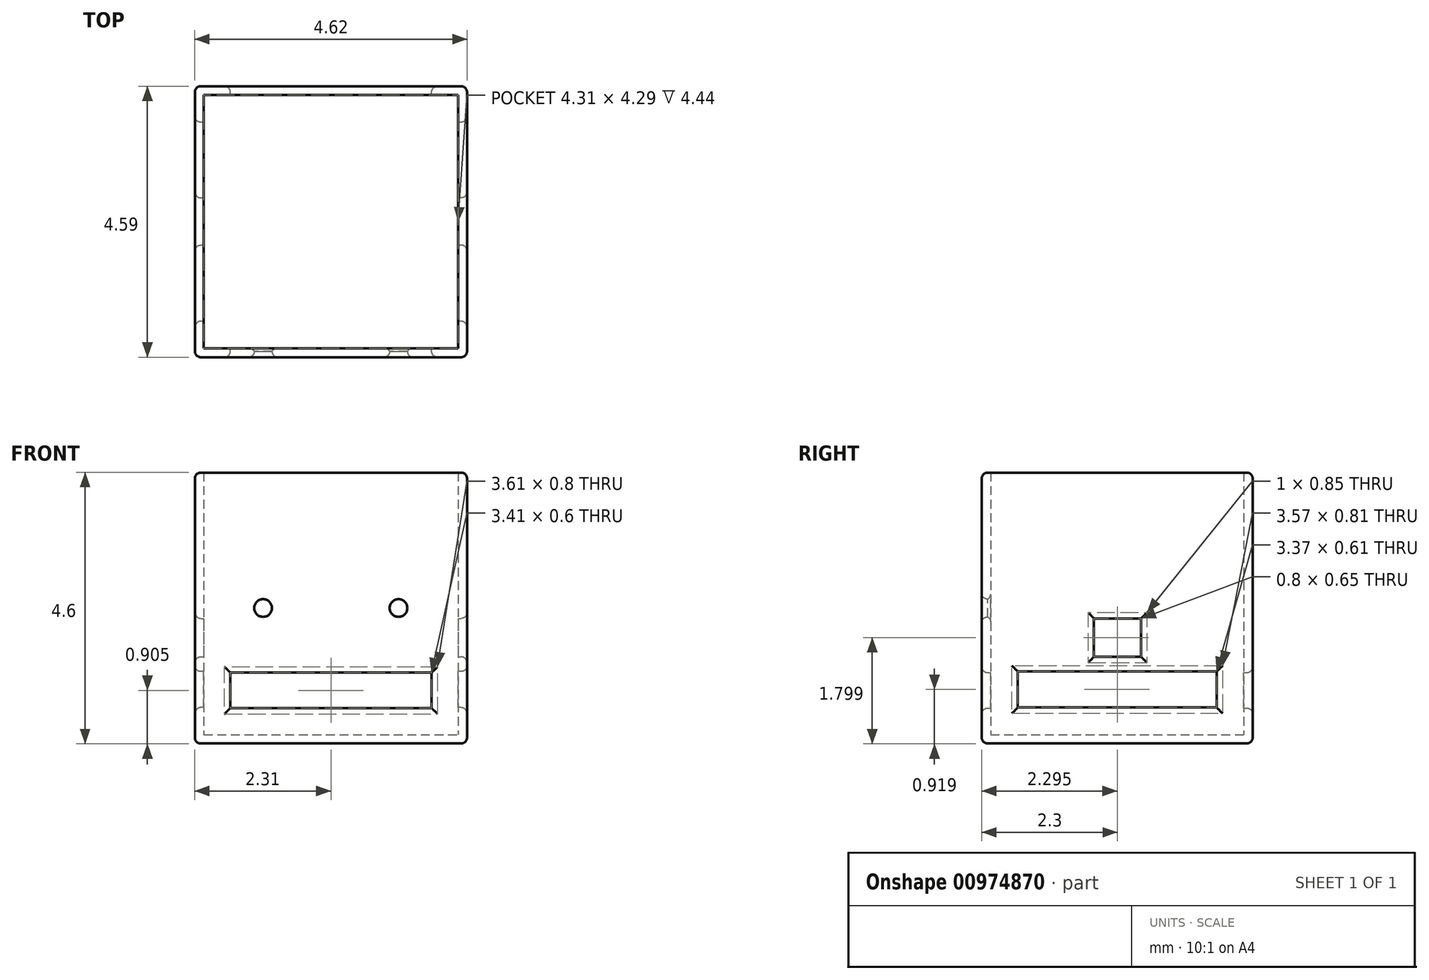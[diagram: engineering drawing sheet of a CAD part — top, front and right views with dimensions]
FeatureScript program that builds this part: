
annotation { "Feature Type Name" : "Feature", "Feature Type Description" : "" }
export const myFeature = defineFeature(function(context is Context, id is Id, definition is map)
    precondition{}
    {
        {
            var Q0;
            Q0=qCreatedBy(makeId("Front.planeOp"),FACE);
            var sketch = newSketch(context, id + "F0", { "sketchPlane" : qUnion([Q0])});
            skLineSegment(sketch, "E0.bottom", {"start": v(-2.3, 2.3) * mm, "end": v(2.3, 2.3) * mm});
            skLineSegment(sketch, "E0.top", {"start": v(-2.3, -2.3) * mm, "end": v(2.3, -2.3) * mm});
            skLineSegment(sketch, "E0.left", {"start": v(-2.3, 2.3) * mm, "end": v(-2.3, -2.3) * mm});
            skLineSegment(sketch, "E0.right", {"start": v(2.3, 2.3) * mm, "end": v(2.3, -2.3) * mm});
            skPoint(sketch, "E0.middle", {"position": v(0, 0) * mm});
            skSolve(sketch);
        }
        {
            var Q0;
            Q0=makeQuery(id+"F0.imprint","IMPRINT",FACE,{"disambiguationData":[TD([[makeQuery(id+"F0.imprint","IMPRINT",EDGE,{"derivedFrom":sQuery(id+"F0.wireOp",EDGE,"E0.bottom")}),-1.0]])]});
            extrude(context, id + "F1", {"entities" : qUnion([Q0]), "depth" : 4.6 * mm, "offsetDistance" : 25.4 * mm});
        }
        {
            var Q0;
            Q0=makeQuery(id+"F1.opExtrude","SWEPT_FACE",FACE,{"disambiguationData":[OSD([sQuery(id+"F0.wireOp",EDGE,"E0.bottom")])]});
            var Q1;
            Q1=makeQuery(id+"F1.opExtrude","SWEPT_BODY",BODY,{"disambiguationData":[OSD([sQuery(id+"F0.wireOp",EDGE,"E0.bottom"),sQuery(id+"F0.wireOp",EDGE,"E0.top"),sQuery(id+"F0.wireOp",EDGE,"E0.left"),sQuery(id+"F0.wireOp",EDGE,"E0.right")])]});
            shell(context, id + "F2", {"entities" : qUnion([Q0]), "parts" : qUnion([Q1]), "thickness" : .15 * mm});
        }
        {
            var Q0;
            Q0=makeQuery(id+"F1.opExtrude","CAP_FACE",FACE,{"disambiguationData":[OSD([sQuery(id+"F0.wireOp",EDGE,"E0.bottom"),sQuery(id+"F0.wireOp",EDGE,"E0.top"),sQuery(id+"F0.wireOp",EDGE,"E0.left"),sQuery(id+"F0.wireOp",EDGE,"E0.right")])],"isStart":false});
            var sketch = newSketch(context, id + "F3", { "sketchPlane" : qUnion([Q0])});
            skCircle(sketch, "E1", {"center": v(1.14, 0) * mm, "radius": 0.15 * mm});
            skCircle(sketch, "E2", {"center": v(-1.15, 0) * mm, "radius": 0.15 * mm});
            skSolve(sketch);
        }
        {
            var Q0;
            Q0 = qSketchRegion(id + "F3", true);
            extrude(context, id + "F4", {"entities" : qUnion([Q0]), "operationType" : NewBodyOperationType.REMOVE, "oppositeDirection" : true, "depth" : .2 * mm, "offsetDistance" : 25.4 * mm});
        }
        {
            var Q0;
            Q0=makeQuery(id+"F1.opExtrude","CAP_FACE",FACE,{"disambiguationData":[OSD([sQuery(id+"F0.wireOp",EDGE,"E0.bottom"),sQuery(id+"F0.wireOp",EDGE,"E0.top"),sQuery(id+"F0.wireOp",EDGE,"E0.left"),sQuery(id+"F0.wireOp",EDGE,"E0.right")])],"isStart":true});
            var sketch = newSketch(context, id + "F5", { "sketchPlane" : qUnion([Q0])});
            skLineSegment(sketch, "E3.bottom", {"start": v(-1.7, -1.1) * mm, "end": v(1.7, -1.1) * mm});
            skLineSegment(sketch, "E3.top", {"start": v(-1.7, -1.7) * mm, "end": v(1.7, -1.7) * mm});
            skLineSegment(sketch, "E3.left", {"start": v(-1.7, -1.1) * mm, "end": v(-1.7, -1.7) * mm});
            skLineSegment(sketch, "E3.right", {"start": v(1.7, -1.1) * mm, "end": v(1.7, -1.7) * mm});
            skPoint(sketch, "E3.middle", {"position": v(0, -1.4) * mm});
            skSolve(sketch);
        }
        {
            var Q0;
            Q0 = qSketchRegion(id + "F5", true);
            extrude(context, id + "F6", {"entities" : qUnion([Q0]), "operationType" : NewBodyOperationType.REMOVE, "oppositeDirection" : true, "depth" : 4.7 * mm, "offsetDistance" : 25.4 * mm});
        }
        {
            var Q0;
            Q0=makeQuery(id+"F1.opExtrude","SWEPT_FACE",FACE,{"disambiguationData":[OSD([sQuery(id+"F0.wireOp",EDGE,"E0.left")])]});
            var sketch = newSketch(context, id + "F7", { "sketchPlane" : qUnion([Q0])});
            skLineSegment(sketch, "E4.bottom", {"start": v(0.6, -1.08) * mm, "end": v(3.98, -1.08) * mm});
            skLineSegment(sketch, "E4.top", {"start": v(0.6, -1.69) * mm, "end": v(3.98, -1.69) * mm});
            skLineSegment(sketch, "E4.left", {"start": v(0.6, -1.08) * mm, "end": v(0.6, -1.69) * mm});
            skLineSegment(sketch, "E4.right", {"start": v(3.98, -1.08) * mm, "end": v(3.98, -1.69) * mm});
            skPoint(sketch, "E4.middle", {"position": v(2.3, -1.38) * mm});
            skSolve(sketch);
        }
        {
            var Q0;
            Q0 = qSketchRegion(id + "F7", true);
            extrude(context, id + "F8", {"entities" : qUnion([Q0]), "operationType" : NewBodyOperationType.REMOVE, "oppositeDirection" : true, "depth" : 4.7 * mm, "offsetDistance" : 25.4 * mm});
        }
        {
            var Q0;
            Q0=makeQuery(id+"F1.opExtrude","SWEPT_FACE",FACE,{"disambiguationData":[OSD([sQuery(id+"F0.wireOp",EDGE,"E0.right")])]});
            var sketch = newSketch(context, id + "F9", { "sketchPlane" : qUnion([Q0])});
            skLineSegment(sketch, "E5.bottom", {"start": v(-2.7, -0.18) * mm, "end": v(-1.9, -0.18) * mm});
            skLineSegment(sketch, "E5.top", {"start": v(-2.7, -0.83) * mm, "end": v(-1.9, -0.83) * mm});
            skLineSegment(sketch, "E5.left", {"start": v(-2.7, -0.18) * mm, "end": v(-2.7, -0.83) * mm});
            skLineSegment(sketch, "E5.right", {"start": v(-1.9, -0.18) * mm, "end": v(-1.9, -0.83) * mm});
            skPoint(sketch, "E5.middle", {"position": v(-2.3, -0.5) * mm});
            skSolve(sketch);
        }
        {
            var Q0;
            Q0 = qSketchRegion(id + "F9", true);
            extrude(context, id + "F10", {"entities" : qUnion([Q0]), "operationType" : NewBodyOperationType.REMOVE, "oppositeDirection" : true, "depth" : 4.7 * mm, "offsetDistance" : 25.4 * mm});
        }
        {
            var Q0;
            Q0=makeQuery(id+"F1.opExtrude","CAP_FACE",FACE,{"disambiguationData":[OSD([sQuery(id+"F0.wireOp",EDGE,"E0.bottom"),sQuery(id+"F0.wireOp",EDGE,"E0.top"),sQuery(id+"F0.wireOp",EDGE,"E0.left"),sQuery(id+"F0.wireOp",EDGE,"E0.right")])],"isStart":false});
            var Q1;
            Q1=makeQuery(id+"F1.opExtrude","SWEPT_FACE",FACE,{"disambiguationData":[OSD([sQuery(id+"F0.wireOp",EDGE,"E0.right")])]});
            var Q2;
            Q2=makeQuery(id+"F1.opExtrude","CAP_FACE",FACE,{"disambiguationData":[OSD([sQuery(id+"F0.wireOp",EDGE,"E0.bottom"),sQuery(id+"F0.wireOp",EDGE,"E0.top"),sQuery(id+"F0.wireOp",EDGE,"E0.left"),sQuery(id+"F0.wireOp",EDGE,"E0.right")])],"isStart":true});
            var Q3;
            Q3=makeQuery(id+"F1.opExtrude","SWEPT_FACE",FACE,{"disambiguationData":[OSD([sQuery(id+"F0.wireOp",EDGE,"E0.left")])]});
            fillet(context, id + "F11", {"entities" : qUnion([Q0, Q1, Q2, Q3]), "radius" : .1 * mm, "tangentPropagation" : true, "allowEdgeOverflow" : false});
        }
        {
            var Q0;
            {var subQ0=sQuery(id+"F0.wireOp",EDGE,"E0.right");var subQ1=sQuery(id+"F0.wireOp",EDGE,"E0.left");var subQ2=sQuery(id+"F0.wireOp",EDGE,"E0.top");var subQ3=sQuery(id+"F0.wireOp",EDGE,"E0.bottom");Q0=makeQuery(id+"F4.boolean.opBoolean","INTERSECT",EDGE,{"derivedFrom":[makeQuery(id+"F2.opShell","OFFSET_FACE",FACE,{"disambiguationData":[OSD([subQ3,subQ2,subQ1,subQ0]),TDD([makeQuery(id+"F1.opExtrude","CAP_FACE",FACE,{"disambiguationData":[OSD([subQ3,subQ2,subQ1,subQ0])],"isStart":false})])]}),makeQuery(id+"F4.opExtrude","SWEPT_FACE",FACE,{"disambiguationData":[OSD([sQuery(id+"F3.wireOp",EDGE,"E1")])]})]});}
            var Q1;
            {var subQ0=sQuery(id+"F0.wireOp",EDGE,"E0.right");var subQ1=sQuery(id+"F0.wireOp",EDGE,"E0.left");var subQ2=sQuery(id+"F0.wireOp",EDGE,"E0.top");var subQ3=sQuery(id+"F0.wireOp",EDGE,"E0.bottom");Q1=makeQuery(id+"F4.boolean.opBoolean","INTERSECT",EDGE,{"derivedFrom":[makeQuery(id+"F2.opShell","OFFSET_FACE",FACE,{"disambiguationData":[OSD([subQ3,subQ2,subQ1,subQ0]),TDD([makeQuery(id+"F1.opExtrude","CAP_FACE",FACE,{"disambiguationData":[OSD([subQ3,subQ2,subQ1,subQ0])],"isStart":false})])]}),makeQuery(id+"F4.opExtrude","SWEPT_FACE",FACE,{"disambiguationData":[OSD([sQuery(id+"F3.wireOp",EDGE,"E2")])]})]});}
            fillet(context, id + "F12", {"entities" : qUnion([Q0, Q1]), "radius" : .1 * mm, "tangentPropagation" : true, "allowEdgeOverflow" : false});
        }
    });
